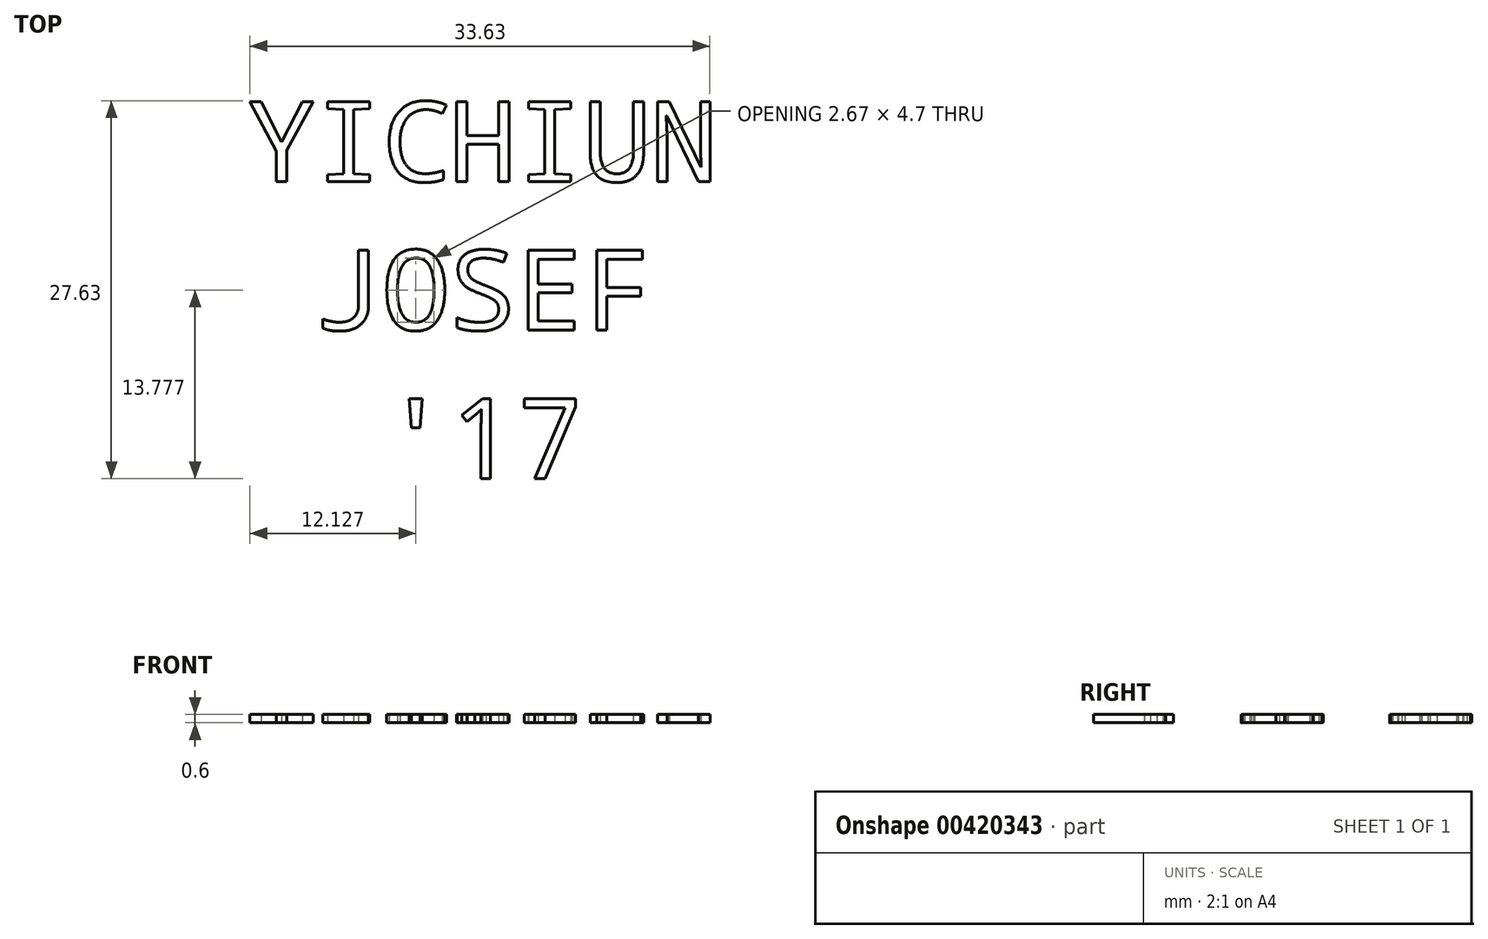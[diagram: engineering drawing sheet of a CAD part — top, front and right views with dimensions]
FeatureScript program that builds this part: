
annotation { "Feature Type Name" : "Feature", "Feature Type Description" : "" }
export const myFeature = defineFeature(function(context is Context, id is Id, definition is map)
    precondition{}
    {
        {
            var Q0;
            Q0=qCreatedBy(makeId("Top.planeOp"),FACE);
            var sketch = newSketch(context, id + "F0", { "sketchPlane" : qUnion([Q0])});
            skText(sketch, "E0", { "text": "YICHIUN\n JOSEF\n  \'17", "fontName": "DroidSansMono.ttf"});
            const initialGuessF0  = {"E0": [-0.01274, 0.0048, 1, 0, 0.00588]};
            skSetInitialGuess(sketch, initialGuessF0);
            skSolve(sketch);
        }
        {
            var Q0;
            Q0 = qSketchRegion(id + "F0", true);
            extrude(context, id + "F1", {"entities" : qUnion([Q0]), "depth" : 0.6 * mm});
        }
    });
